# Revit family: P210059AX-018_ACR4303MFW
name_source: partatom
category: Specialty Equipment
units: mm (PartAtom-declared; Revit-internal decimal feet)

## family parameters
Always vertical = Yes
Cut with Voids When Loaded = No
Enable Cutting in Views = No
Maintain Annotation Orientation = No
Part Type = Normal
Room Calculation Point = No
Round Connector Dimension = Use Diameter
Shared = No
Work Plane-Based = No

## types (1)
- ACR4303MFW
    Accent Material = ARCAT - Plastic - Gray
    Amps = 0 A
    Back Panel Material = ARCAT - Metal - Aluminum
    Body Material = ARCAT - Metal - Steel - White
    Clearance Material = ARCAT - Clearance
    Cooking Grid Material = ARCAT - Metal - Steel - Black
    Cooktop Base Material = ARCAT - Metal - Steel - Stainless
    Default Elevation = 0"
    Depth = 27 3/4"
    Description = 30-inch Electric Range with Bake Assist Temps
    Dimension Guide = https://access.whirlpool.com Guide&sku=ACR4303MFB&language=EN
    Display Panel Material = ARCAT - Glass - Black
    Door Material = ARCAT - Metal - Steel - White
    Family Name = Electric range
    Feature 1 = Large Oven Capacity (4.8 cu. ft.)
    Feature 2 = Versatile Cooktop
    Feature 3 = Bake Assist Temps
    Glass Material = ARCAT - Glass -Tempered - Black
    Handle Material = ARCAT - Metal - Steel - White
    Height = 46 7/8"
    Installation-Fabrication = https://www.whirlpool.com
    Knob Material = ARCAT - Plastic - White
    Leg Material = ARCAT - Plastic - Black
    Manufacturer = Amana
    Model = ACR4303MFW
    Voltage = 0 V
    Width = 29 7/8"

## geometry (parser evidence)
native form markers: Sweep x5
no freeform markers — native parametric forms only
